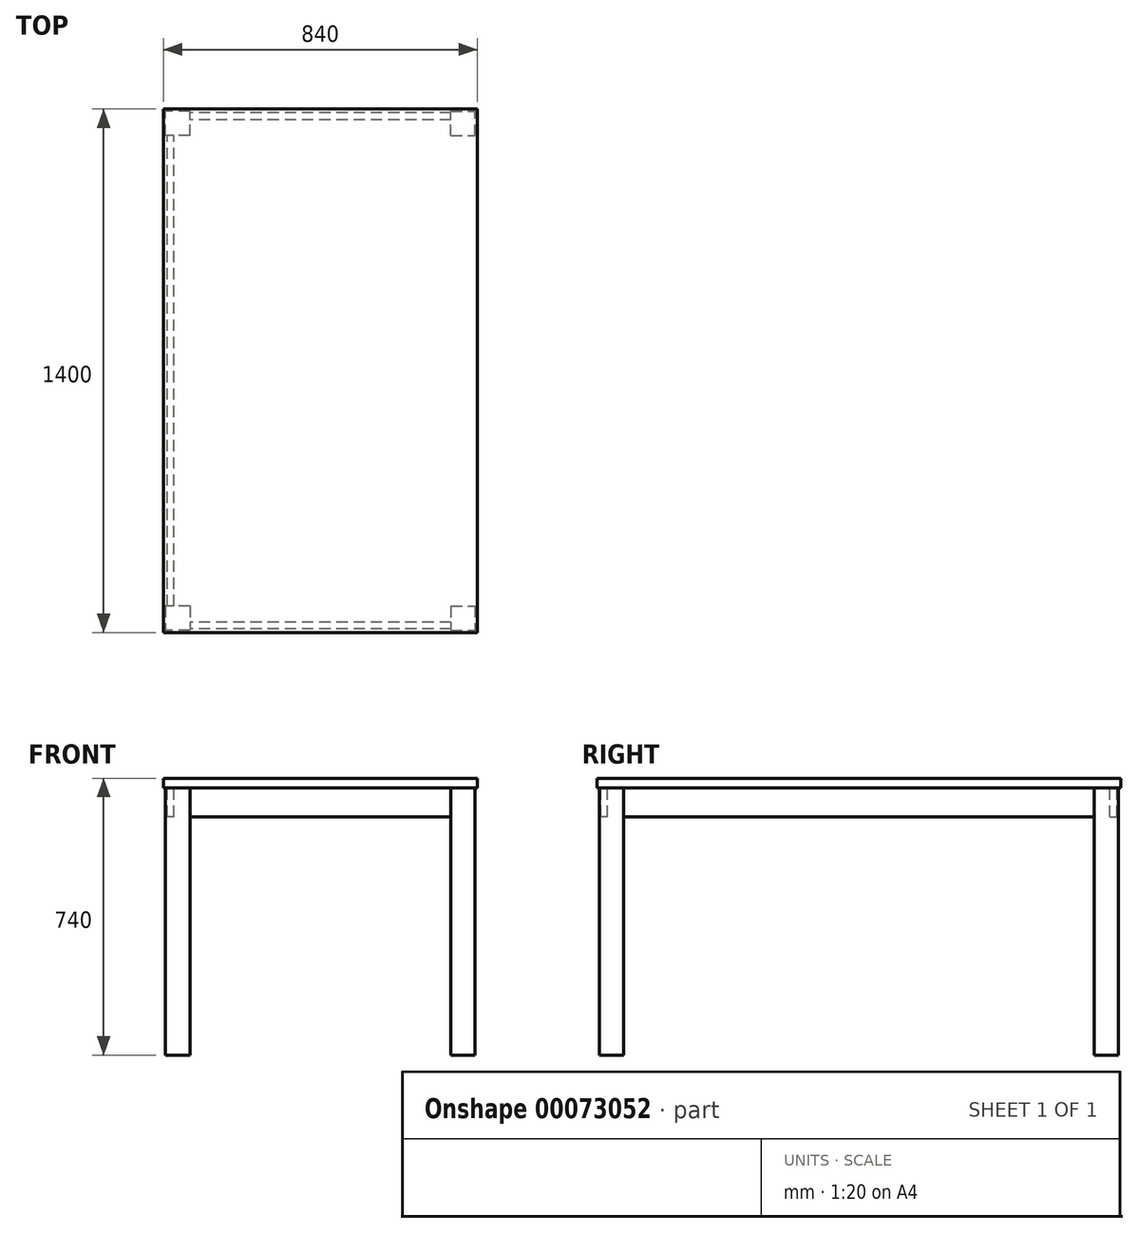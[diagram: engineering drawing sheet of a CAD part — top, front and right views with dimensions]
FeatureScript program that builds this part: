
annotation { "Feature Type Name" : "Feature", "Feature Type Description" : "" }
export const myFeature = defineFeature(function(context is Context, id is Id, definition is map)
    precondition{}
    {
        {
            var Q0;
            Q0=qCreatedBy(makeId("Top.planeOp"),FACE);
            var sketch = newSketch(context, id + "F0", { "sketchPlane" : qUnion([Q0])});
            skLineSegment(sketch, "E0.bottom", {"start": v(420, -700) * mm, "end": v(-420, -700) * mm});
            skLineSegment(sketch, "E0.top", {"start": v(420, 700) * mm, "end": v(-420, 700) * mm});
            skLineSegment(sketch, "E0.left", {"start": v(420, -700) * mm, "end": v(420, 700) * mm});
            skLineSegment(sketch, "E0.right", {"start": v(-420, -700) * mm, "end": v(-420, 700) * mm});
            skPoint(sketch, "E0.middle", {"position": v(0, 0) * mm});
            skSolve(sketch);
        }
        {
            var Q0;
            Q0=makeQuery(id+"F0.imprint","IMPRINT",FACE,{"disambiguationData":[TD([[makeQuery(id+"F0.imprint","IMPRINT",EDGE,{"derivedFrom":sQuery(id+"F0.wireOp",EDGE,"E0.bottom")}),-1.0]])]});
            extrude(context, id + "F1", {"entities" : qUnion([Q0]), "depth" : 25 * mm});
        }
        {
            var Q0;
            Q0=makeQuery(id+"F1.opExtrude","CAP_FACE",FACE,{"disambiguationData":[OSD([sQuery(id+"F0.wireOp",EDGE,"E0.bottom"),sQuery(id+"F0.wireOp",EDGE,"E0.top"),sQuery(id+"F0.wireOp",EDGE,"E0.left"),sQuery(id+"F0.wireOp",EDGE,"E0.right")])],"isStart":true});
            var sketch = newSketch(context, id + "F2", { "sketchPlane" : qUnion([Q0])});
            skLineSegment(sketch, "E1", {"start": v(0, 0) * mm, "end": v(126.46, 0) * mm, "construction": true});
            skLineSegment(sketch, "E2", {"start": v(0, 0) * mm, "end": v(0, -169.7) * mm, "construction": true});
            skLineSegment(sketch, "E3.bottom", {"start": v(349, 629) * mm, "end": v(414, 629) * mm});
            skLineSegment(sketch, "E3.top", {"start": v(349, 694) * mm, "end": v(414, 694) * mm});
            skLineSegment(sketch, "E3.left", {"start": v(349, 629) * mm, "end": v(349, 694) * mm});
            skLineSegment(sketch, "E3.right", {"start": v(414, 629) * mm, "end": v(414, 694) * mm});
            skPoint(sketch, "E3.middle", {"position": v(381.5, 661.5) * mm});
            skLineSegment(sketch, "E4.MirrorCS", {"start": v(414, -629) * mm, "end": v(414, -694) * mm});
            skLineSegment(sketch, "E5.MirrorCS", {"start": v(349, -629) * mm, "end": v(349, -694) * mm});
            skLineSegment(sketch, "E6.MirrorCS", {"start": v(349, -629) * mm, "end": v(414, -629) * mm});
            skLineSegment(sketch, "E7.MirrorCS", {"start": v(349, -694) * mm, "end": v(414, -694) * mm});
            skPoint(sketch, "E8.MirrorP", {"position": v(381.5, -661.5) * mm});
            skLineSegment(sketch, "E9.MirrorCS", {"start": v(-414, 629) * mm, "end": v(-414, 694) * mm});
            skLineSegment(sketch, "E10.MirrorCS", {"start": v(-414, -629) * mm, "end": v(-414, -694) * mm});
            skLineSegment(sketch, "E11.MirrorCS", {"start": v(-349, 629) * mm, "end": v(-349, 694) * mm});
            skLineSegment(sketch, "E12.MirrorCS", {"start": v(-349, 694) * mm, "end": v(-414, 694) * mm});
            skLineSegment(sketch, "E13.MirrorCS", {"start": v(-349, 629) * mm, "end": v(-414, 629) * mm});
            skLineSegment(sketch, "E14.MirrorCS", {"start": v(-349, -629) * mm, "end": v(-349, -694) * mm});
            skLineSegment(sketch, "E15.MirrorCS", {"start": v(-349, -694) * mm, "end": v(-414, -694) * mm});
            skLineSegment(sketch, "E16.MirrorCS", {"start": v(-349, -629) * mm, "end": v(-414, -629) * mm});
            skPoint(sketch, "E17.MirrorP", {"position": v(-381.5, -661.5) * mm});
            skPoint(sketch, "E18.MirrorP", {"position": v(-381.5, 661.5) * mm});
            skLineSegment(sketch, "E19.bottom", {"start": v(410, 629) * mm, "end": v(392, 629) * mm});
            skLineSegment(sketch, "E19.top", {"start": v(410, -629) * mm, "end": v(392, -629) * mm});
            skLineSegment(sketch, "E19.left", {"start": v(410, 629) * mm, "end": v(410, -629) * mm});
            skLineSegment(sketch, "E19.right", {"start": v(392, 629) * mm, "end": v(392, -629) * mm});
            skLineSegment(sketch, "E20.bottom", {"start": v(349, -672) * mm, "end": v(-349, -672) * mm});
            skLineSegment(sketch, "E20.top", {"start": v(349, -690) * mm, "end": v(-349, -690) * mm});
            skLineSegment(sketch, "E20.left", {"start": v(349, -672) * mm, "end": v(349, -690) * mm});
            skLineSegment(sketch, "E20.right", {"start": v(-349, -672) * mm, "end": v(-349, -690) * mm});
            skLineSegment(sketch, "E21.MirrorCS", {"start": v(-392, 629) * mm, "end": v(-392, -629) * mm});
            skLineSegment(sketch, "E22.MirrorCS", {"start": v(-410, 629) * mm, "end": v(-410, -629) * mm});
            skLineSegment(sketch, "E23.MirrorCS", {"start": v(349, 672) * mm, "end": v(-349, 672) * mm});
            skLineSegment(sketch, "E24.MirrorCS", {"start": v(349, 690) * mm, "end": v(-349, 690) * mm});
            skSolve(sketch);
        }
        {
            var Q0;
            Q0=makeQuery(id+"F2.imprint","IMPRINT",FACE,{"disambiguationData":[TD([[makeQuery(id+"F2.imprint","IMPRINT",EDGE,{"derivedFrom":sQuery(id+"F2.wireOp",EDGE,"E3.bottom")}),1.0]])]});
            var Q1;
            Q1=makeQuery(id+"F2.imprint","IMPRINT",FACE,{"disambiguationData":[TD([[makeQuery(id+"F2.imprint","IMPRINT",EDGE,{"derivedFrom":sQuery(id+"F2.wireOp",EDGE,"E4.MirrorCS")}),-1.0]])]});
            var Q2;
            Q2=makeQuery(id+"F2.imprint","IMPRINT",FACE,{"disambiguationData":[TD([[makeQuery(id+"F2.imprint","IMPRINT",EDGE,{"derivedFrom":sQuery(id+"F2.wireOp",EDGE,"E10.MirrorCS")}),1.0]])]});
            var Q3;
            Q3=makeQuery(id+"F2.imprint","IMPRINT",FACE,{"disambiguationData":[TD([[makeQuery(id+"F2.imprint","IMPRINT",EDGE,{"derivedFrom":sQuery(id+"F2.wireOp",EDGE,"E9.MirrorCS")}),-1.0]])]});
            extrude(context, id + "F3", {"entities" : qUnion([Q0, Q1, Q2, Q3]), "operationType" : NewBodyOperationType.ADD, "depth" : 715 * mm});
        }
        {
            var Q0;
            Q0=makeQuery(id+"F2.imprint","IMPRINT",FACE,{"disambiguationData":[TD([[makeQuery(id+"F2.imprint","IMPRINT",EDGE,{"derivedFrom":sQuery(id+"F2.wireOp",EDGE,"E19.bottom")}),1.0]])]});
            var Q1;
            {var subQ0=sQuery(id+"F2.wireOp",EDGE,"E23.MirrorCS");Q1=makeQuery(id+"F2.imprint","IMPRINT",FACE,{"disambiguationData":[TD([[makeQuery(id+"F2.imprint","IMPRINT",EDGE,{"derivedFrom":subQ0}),-1.0]])]});}
            var Q2;
            {var subQ0=sQuery(id+"F2.wireOp",EDGE,"E21.MirrorCS");Q2=makeQuery(id+"F2.imprint","IMPRINT",FACE,{"disambiguationData":[TD([[makeQuery(id+"F2.imprint","IMPRINT",EDGE,{"derivedFrom":subQ0}),-1.0]])]});}
            var Q3;
            Q3=makeQuery(id+"F2.imprint","IMPRINT",FACE,{"disambiguationData":[TD([[makeQuery(id+"F2.imprint","IMPRINT",EDGE,{"derivedFrom":sQuery(id+"F2.wireOp",EDGE,"E20.bottom")}),1.0]])]});
            extrude(context, id + "F4", {"entities" : qUnion([Q0, Q1, Q2, Q3]), "operationType" : NewBodyOperationType.ADD, "depth" : 78 * mm});
        }
    });
